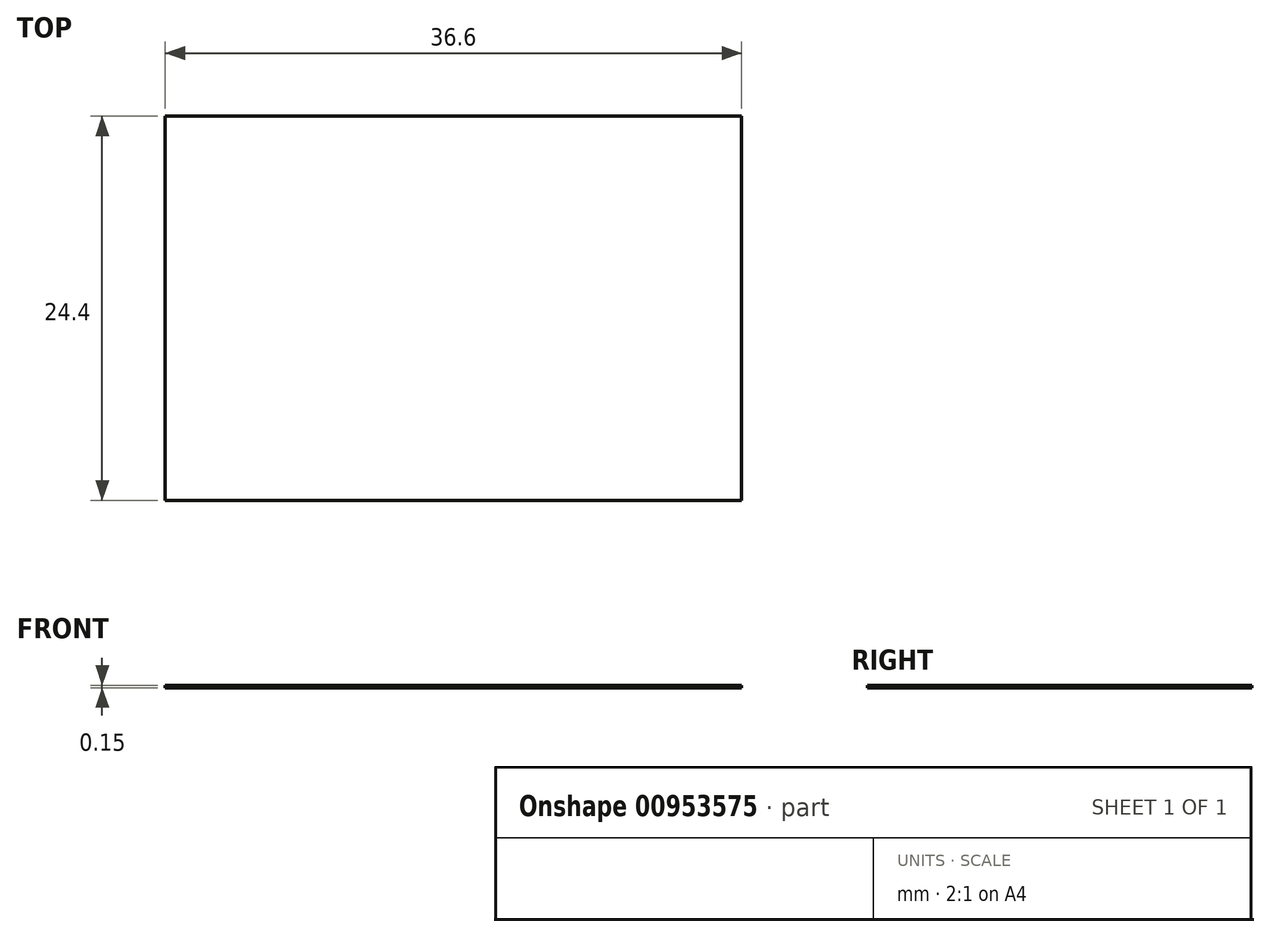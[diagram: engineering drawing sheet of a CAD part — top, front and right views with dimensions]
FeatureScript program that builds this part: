
annotation { "Feature Type Name" : "Feature", "Feature Type Description" : "" }
export const myFeature = defineFeature(function(context is Context, id is Id, definition is map)
    precondition{}
    {
        {
            var Q0;
            Q0=qCreatedBy(makeId("Top.planeOp"),FACE);
            var sketch = newSketch(context, id + "F0", { "sketchPlane" : qUnion([Q0])});
            skLineSegment(sketch, "E0.bottom", {"start": v(1.19, 0.06) * mm, "end": v(37.79, 0.06) * mm});
            skLineSegment(sketch, "E0.top", {"start": v(1.19, -24.34) * mm, "end": v(37.79, -24.34) * mm});
            skLineSegment(sketch, "E0.left", {"start": v(1.19, 0.06) * mm, "end": v(1.19, -24.34) * mm});
            skLineSegment(sketch, "E0.right", {"start": v(37.79, 0.06) * mm, "end": v(37.79, -24.34) * mm});
            skPoint(sketch, "E1", {"position": v(1.95, 0.06) * mm});
            skPoint(sketch, "E2", {"position": v(37.03, 0.06) * mm});
            skPoint(sketch, "E3", {"position": v(1.19, -23.58) * mm});
            skPoint(sketch, "E4", {"position": v(1.19, -0.7) * mm});
            skPoint(sketch, "E5", {"position": v(13.39, 0.06) * mm});
            skPoint(sketch, "E6", {"position": v(25.59, -24.34) * mm});
            skPoint(sketch, "E7", {"position": v(25.59, 0.06) * mm});
            skPoint(sketch, "E8", {"position": v(37.79, -24.34) * mm});
            skLineSegment(sketch, "E9", {"start": v(1.19, -0.7) * mm, "end": v(37.79, -0.7) * mm});
            skLineSegment(sketch, "E10", {"start": v(1.19, -23.58) * mm, "end": v(37.79, -23.58) * mm});
            skLineSegment(sketch, "E11", {"start": v(1.95, 0.06) * mm, "end": v(1.95, -24.34) * mm});
            skLineSegment(sketch, "E12", {"start": v(37.03, 0.06) * mm, "end": v(37.03, -24.34) * mm});
            skPoint(sketch, "E13", {"position": v(1.19, -12.14) * mm});
            skPoint(sketch, "E14", {"position": v(37.79, -12.14) * mm});
            skLineSegment(sketch, "E15", {"start": v(1.95, -12.14) * mm, "end": v(25.59, -12.14) * mm});
            skLineSegment(sketch, "E16", {"start": v(25.59, -24.34) * mm, "end": v(25.59, -0.7) * mm});
            skLineSegment(sketch, "E17", {"start": v(25.59, -0.7) * mm, "end": v(25.59, 0.06) * mm});
            skLineSegment(sketch, "E18", {"start": v(1.19, -12.14) * mm, "end": v(1.95, -12.14) * mm});
            skLineSegment(sketch, "E19.trimOffspring", {"start": v(37.03, -12.14) * mm, "end": v(37.79, -12.14) * mm});
            skPoint(sketch, "E20", {"position": v(37.79, -11.64) * mm});
            skPoint(sketch, "E21", {"position": v(37.79, -12.64) * mm});
            skLineSegment(sketch, "E22", {"start": v(13.39, 0.06) * mm, "end": v(12.81, -24.34) * mm});
            skPoint(sketch, "E23", {"position": v(1.69, 0.06) * mm});
            skPoint(sketch, "E24", {"position": v(12.89, 0.06) * mm});
            skPoint(sketch, "E25", {"position": v(13.89, 0.06) * mm});
            skPoint(sketch, "E26", {"position": v(25.09, 0.06) * mm});
            skPoint(sketch, "E27", {"position": v(26.09, 0.06) * mm});
            skPoint(sketch, "E28", {"position": v(37.29, 0.06) * mm});
            skPoint(sketch, "E29", {"position": v(37.79, -1.2) * mm});
            skPoint(sketch, "E30", {"position": v(37.79, -23.08) * mm});
            skLineSegment(sketch, "E31", {"start": v(1.69, 0.06) * mm, "end": v(1.69, -24.34) * mm});
            skLineSegment(sketch, "E32", {"start": v(12.89, 0.06) * mm, "end": v(12.31, -24.34) * mm});
            skLineSegment(sketch, "E33", {"start": v(13.89, 0.06) * mm, "end": v(13.31, -24.34) * mm});
            skLineSegment(sketch, "E34", {"start": v(25.09, 0.06) * mm, "end": v(25.09, -24.34) * mm});
            skLineSegment(sketch, "E35", {"start": v(26.09, 0.06) * mm, "end": v(26.09, -24.34) * mm});
            skLineSegment(sketch, "E36", {"start": v(37.29, 0.06) * mm, "end": v(37.29, -24.34) * mm});
            skLineSegment(sketch, "E37", {"start": v(37.79, -1.2) * mm, "end": v(1.19, -1.2) * mm});
            skLineSegment(sketch, "E38", {"start": v(37.79, -23.08) * mm, "end": v(1.19, -23.08) * mm});
            skSolve(sketch);
        }
        {
            var Q0;
            {var subQ0=sQuery(id+"F0.wireOp",EDGE,"E18");var subQ1=sQuery(id+"F0.wireOp",EDGE,"E0.left");var subQ2=makeQuery(id+"F0.imprint","INTERSECT",VERTEX,{"derivedFrom":[subQ1,subQ0]});Q0=makeQuery(id+"F0.imprint","IMPRINT",FACE,{"disambiguationData":[TD([[makeQuery(id+"F0.imprint","IMPRINT",EDGE,{"disambiguationData":[TD([[subQ2,-1.0]])],"derivedFrom":subQ1}),1.0]])]});}
            var Q1;
            {var subQ0=sQuery(id+"F0.wireOp",EDGE,"E32");var subQ1=sQuery(id+"F0.wireOp",EDGE,"E9");var subQ2=makeQuery(id+"F0.imprint","INTERSECT",VERTEX,{"derivedFrom":[subQ1,subQ0]});Q1=makeQuery(id+"F0.imprint","IMPRINT",FACE,{"disambiguationData":[TD([[makeQuery(id+"F0.imprint","IMPRINT",EDGE,{"disambiguationData":[TD([[subQ2,-1.0]])],"derivedFrom":subQ1}),-1.0]])]});}
            var Q2;
            {var subQ0=sQuery(id+"F0.wireOp",EDGE,"E12");var subQ1=sQuery(id+"F0.wireOp",EDGE,"E0.bottom");var subQ2=makeQuery(id+"F0.imprint","INTERSECT",VERTEX,{"derivedFrom":[subQ1,subQ0]});Q2=makeQuery(id+"F0.imprint","IMPRINT",FACE,{"disambiguationData":[TD([[makeQuery(id+"F0.imprint","IMPRINT",EDGE,{"disambiguationData":[TD([[subQ2,1.0]])],"derivedFrom":subQ1}),-1.0]])]});}
            var Q3;
            {var subQ0=sQuery(id+"F0.wireOp",EDGE,"E12");var subQ1=sQuery(id+"F0.wireOp",EDGE,"E0.top");var subQ2=makeQuery(id+"F0.imprint","INTERSECT",VERTEX,{"derivedFrom":[subQ1,subQ0]});Q3=makeQuery(id+"F0.imprint","IMPRINT",FACE,{"disambiguationData":[TD([[makeQuery(id+"F0.imprint","IMPRINT",EDGE,{"disambiguationData":[TD([[subQ2,1.0]])],"derivedFrom":subQ1}),1.0]])]});}
            var Q4;
            {var subQ0=sQuery(id+"F0.wireOp",EDGE,"E15");var subQ5=sQuery(id+"F0.wireOp",EDGE,"E32");var subQ6=makeQuery(id+"F0.imprint","INTERSECT",VERTEX,{"derivedFrom":[subQ0,subQ5]});Q4=makeQuery(id+"F0.imprint","IMPRINT",FACE,{"disambiguationData":[TD([[makeQuery(id+"F0.imprint","IMPRINT",EDGE,{"disambiguationData":[TD([[subQ6,-1.0]])],"derivedFrom":subQ5}),-1.0]])]});}
            var Q5;
            {var subQ0=sQuery(id+"F0.wireOp",EDGE,"E16");var subQ1=sQuery(id+"F0.wireOp",EDGE,"E15");var subQ2=makeQuery(id+"F0.imprint","INTERSECT",VERTEX,{"derivedFrom":[subQ1,subQ0]});Q5=makeQuery(id+"F0.imprint","IMPRINT",FACE,{"disambiguationData":[TD([[makeQuery(id+"F0.imprint","IMPRINT",EDGE,{"disambiguationData":[TD([[subQ2,1.0]])],"derivedFrom":subQ1}),-1.0]])]});}
            var Q6;
            {var subQ0=sQuery(id+"F0.wireOp",EDGE,"E22");var subQ1=sQuery(id+"F0.wireOp",EDGE,"E15");var subQ2=makeQuery(id+"F0.imprint","INTERSECT",VERTEX,{"derivedFrom":[subQ1,subQ0]});Q6=makeQuery(id+"F0.imprint","IMPRINT",FACE,{"disambiguationData":[TD([[makeQuery(id+"F0.imprint","IMPRINT",EDGE,{"disambiguationData":[TD([[subQ2,-1.0]])],"derivedFrom":subQ1}),1.0]])]});}
            var Q7;
            {var subQ0=sQuery(id+"F0.wireOp",EDGE,"E18");var subQ1=sQuery(id+"F0.wireOp",EDGE,"E0.left");var subQ2=makeQuery(id+"F0.imprint","INTERSECT",VERTEX,{"derivedFrom":[subQ1,subQ0]});Q7=makeQuery(id+"F0.imprint","IMPRINT",FACE,{"disambiguationData":[TD([[makeQuery(id+"F0.imprint","IMPRINT",EDGE,{"disambiguationData":[TD([[subQ2,1.0]])],"derivedFrom":subQ1}),1.0]])]});}
            var Q8;
            {var subQ0=sQuery(id+"F0.wireOp",EDGE,"E22");var subQ1=sQuery(id+"F0.wireOp",EDGE,"E15");var subQ2=makeQuery(id+"F0.imprint","INTERSECT",VERTEX,{"derivedFrom":[subQ1,subQ0]});Q8=makeQuery(id+"F0.imprint","IMPRINT",FACE,{"disambiguationData":[TD([[makeQuery(id+"F0.imprint","IMPRINT",EDGE,{"disambiguationData":[TD([[subQ2,-1.0]])],"derivedFrom":subQ1}),-1.0]])]});}
            var Q9;
            {var subQ0=sQuery(id+"F0.wireOp",EDGE,"E11");var subQ1=sQuery(id+"F0.wireOp",EDGE,"E9");var subQ2=makeQuery(id+"F0.imprint","INTERSECT",VERTEX,{"derivedFrom":[subQ1,subQ0]});Q9=makeQuery(id+"F0.imprint","IMPRINT",FACE,{"disambiguationData":[TD([[makeQuery(id+"F0.imprint","IMPRINT",EDGE,{"disambiguationData":[TD([[subQ2,-1.0]])],"derivedFrom":subQ1}),-1.0]])]});}
            var Q10;
            {var subQ0=sQuery(id+"F0.wireOp",EDGE,"E11");var subQ1=sQuery(id+"F0.wireOp",EDGE,"E0.bottom");var subQ2=makeQuery(id+"F0.imprint","INTERSECT",VERTEX,{"derivedFrom":[subQ1,subQ0]});Q10=makeQuery(id+"F0.imprint","IMPRINT",FACE,{"disambiguationData":[TD([[makeQuery(id+"F0.imprint","IMPRINT",EDGE,{"disambiguationData":[TD([[subQ2,-1.0]])],"derivedFrom":subQ1}),-1.0]])]});}
            var Q11;
            {var subQ0=sQuery(id+"F0.wireOp",EDGE,"E32");var subQ1=sQuery(id+"F0.wireOp",EDGE,"E10");var subQ2=makeQuery(id+"F0.imprint","INTERSECT",VERTEX,{"derivedFrom":[subQ1,subQ0]});Q11=makeQuery(id+"F0.imprint","IMPRINT",FACE,{"disambiguationData":[TD([[makeQuery(id+"F0.imprint","IMPRINT",EDGE,{"disambiguationData":[TD([[subQ2,-1.0]])],"derivedFrom":subQ1}),1.0]])]});}
            var Q12;
            {var subQ0=sQuery(id+"F0.wireOp",EDGE,"E33");var subQ1=sQuery(id+"F0.wireOp",EDGE,"E0.top");var subQ2=makeQuery(id+"F0.imprint","INTERSECT",VERTEX,{"derivedFrom":[subQ1,subQ0]});Q12=makeQuery(id+"F0.imprint","IMPRINT",FACE,{"disambiguationData":[TD([[makeQuery(id+"F0.imprint","IMPRINT",EDGE,{"disambiguationData":[TD([[subQ2,-1.0]])],"derivedFrom":subQ1}),1.0]])]});}
            var Q13;
            {var subQ0=sQuery(id+"F0.wireOp",EDGE,"E19.trimOffspring");var subQ1=sQuery(id+"F0.wireOp",EDGE,"E0.right");var subQ2=makeQuery(id+"F0.imprint","INTERSECT",VERTEX,{"derivedFrom":[subQ1,subQ0]});Q13=makeQuery(id+"F0.imprint","IMPRINT",FACE,{"disambiguationData":[TD([[makeQuery(id+"F0.imprint","IMPRINT",EDGE,{"disambiguationData":[TD([[subQ2,-1.0]])],"derivedFrom":subQ1}),-1.0]])]});}
            var Q14;
            {var subQ0=sQuery(id+"F0.wireOp",EDGE,"E22");var subQ1=sQuery(id+"F0.wireOp",EDGE,"E0.top");var subQ2=makeQuery(id+"F0.imprint","INTERSECT",VERTEX,{"derivedFrom":[subQ1,subQ0]});Q14=makeQuery(id+"F0.imprint","IMPRINT",FACE,{"disambiguationData":[TD([[makeQuery(id+"F0.imprint","IMPRINT",EDGE,{"disambiguationData":[TD([[subQ2,1.0]])],"derivedFrom":subQ1}),1.0]])]});}
            var Q15;
            {var subQ0=sQuery(id+"F0.wireOp",EDGE,"E11");var subQ1=sQuery(id+"F0.wireOp",EDGE,"E0.top");var subQ2=makeQuery(id+"F0.imprint","INTERSECT",VERTEX,{"derivedFrom":[subQ1,subQ0]});Q15=makeQuery(id+"F0.imprint","IMPRINT",FACE,{"disambiguationData":[TD([[makeQuery(id+"F0.imprint","IMPRINT",EDGE,{"disambiguationData":[TD([[subQ2,-1.0]])],"derivedFrom":subQ1}),1.0]])]});}
            var Q16;
            {var subQ0=sQuery(id+"F0.wireOp",EDGE,"E33");var subQ1=sQuery(id+"F0.wireOp",EDGE,"E0.bottom");var subQ2=makeQuery(id+"F0.imprint","INTERSECT",VERTEX,{"derivedFrom":[subQ1,subQ0]});Q16=makeQuery(id+"F0.imprint","IMPRINT",FACE,{"disambiguationData":[TD([[makeQuery(id+"F0.imprint","IMPRINT",EDGE,{"disambiguationData":[TD([[subQ2,-1.0]])],"derivedFrom":subQ1}),-1.0]])]});}
            var Q17;
            {var subQ1=sQuery(id+"F0.wireOp",EDGE,"E12");var subQ8=makeQuery(id+"F0.imprint","INTERSECT",VERTEX,{"derivedFrom":[subQ1,sQuery(id+"F0.wireOp",EDGE,"E19.trimOffspring")]});Q17=makeQuery(id+"F0.imprint","IMPRINT",FACE,{"disambiguationData":[TD([[makeQuery(id+"F0.imprint","IMPRINT",EDGE,{"disambiguationData":[TD([[subQ8,1.0]])],"derivedFrom":subQ1}),-1.0]])]});}
            var Q18;
            {var subQ1=sQuery(id+"F0.wireOp",EDGE,"E16");var subQ8=makeQuery(id+"F0.imprint","INTERSECT",VERTEX,{"derivedFrom":[sQuery(id+"F0.wireOp",EDGE,"E15"),subQ1]});Q18=makeQuery(id+"F0.imprint","IMPRINT",FACE,{"disambiguationData":[TD([[makeQuery(id+"F0.imprint","IMPRINT",EDGE,{"disambiguationData":[TD([[subQ8,1.0]])],"derivedFrom":subQ1}),-1.0]])]});}
            var Q19;
            {var subQ0=sQuery(id+"F0.wireOp",EDGE,"E15");var subQ5=sQuery(id+"F0.wireOp",EDGE,"E32");var subQ6=makeQuery(id+"F0.imprint","INTERSECT",VERTEX,{"derivedFrom":[subQ0,subQ5]});Q19=makeQuery(id+"F0.imprint","IMPRINT",FACE,{"disambiguationData":[TD([[makeQuery(id+"F0.imprint","IMPRINT",EDGE,{"disambiguationData":[TD([[subQ6,1.0]])],"derivedFrom":subQ5}),-1.0]])]});}
            var Q20;
            {var subQ0=sQuery(id+"F0.wireOp",EDGE,"E16");var subQ1=sQuery(id+"F0.wireOp",EDGE,"E15");var subQ2=makeQuery(id+"F0.imprint","INTERSECT",VERTEX,{"derivedFrom":[subQ1,subQ0]});Q20=makeQuery(id+"F0.imprint","IMPRINT",FACE,{"disambiguationData":[TD([[makeQuery(id+"F0.imprint","IMPRINT",EDGE,{"disambiguationData":[TD([[subQ2,1.0]])],"derivedFrom":subQ1}),1.0]])]});}
            var Q21;
            {var subQ0=sQuery(id+"F0.wireOp",EDGE,"E16");var subQ1=sQuery(id+"F0.wireOp",EDGE,"E10");var subQ2=makeQuery(id+"F0.imprint","INTERSECT",VERTEX,{"derivedFrom":[subQ1,subQ0]});Q21=makeQuery(id+"F0.imprint","IMPRINT",FACE,{"disambiguationData":[TD([[makeQuery(id+"F0.imprint","IMPRINT",EDGE,{"disambiguationData":[TD([[subQ2,-1.0]])],"derivedFrom":subQ1}),1.0]])]});}
            var Q22;
            {var subQ0=sQuery(id+"F0.wireOp",EDGE,"E35");var subQ1=sQuery(id+"F0.wireOp",EDGE,"E9");var subQ2=makeQuery(id+"F0.imprint","INTERSECT",VERTEX,{"derivedFrom":[subQ1,subQ0]});Q22=makeQuery(id+"F0.imprint","IMPRINT",FACE,{"disambiguationData":[TD([[makeQuery(id+"F0.imprint","IMPRINT",EDGE,{"disambiguationData":[TD([[subQ2,-1.0]])],"derivedFrom":subQ1}),-1.0]])]});}
            var Q23;
            {var subQ0=sQuery(id+"F0.wireOp",EDGE,"E32");var subQ1=sQuery(id+"F0.wireOp",EDGE,"E15");var subQ2=makeQuery(id+"F0.imprint","INTERSECT",VERTEX,{"derivedFrom":[subQ1,subQ0]});Q23=makeQuery(id+"F0.imprint","IMPRINT",FACE,{"disambiguationData":[TD([[makeQuery(id+"F0.imprint","IMPRINT",EDGE,{"disambiguationData":[TD([[subQ2,-1.0]])],"derivedFrom":subQ1}),-1.0]])]});}
            var Q24;
            {var subQ0=sQuery(id+"F0.wireOp",EDGE,"E19.trimOffspring");var subQ1=sQuery(id+"F0.wireOp",EDGE,"E0.right");var subQ2=makeQuery(id+"F0.imprint","INTERSECT",VERTEX,{"derivedFrom":[subQ1,subQ0]});Q24=makeQuery(id+"F0.imprint","IMPRINT",FACE,{"disambiguationData":[TD([[makeQuery(id+"F0.imprint","IMPRINT",EDGE,{"disambiguationData":[TD([[subQ2,1.0]])],"derivedFrom":subQ1}),-1.0]])]});}
            var Q25;
            {var subQ0=sQuery(id+"F0.wireOp",EDGE,"E22");var subQ1=sQuery(id+"F0.wireOp",EDGE,"E9");var subQ2=makeQuery(id+"F0.imprint","INTERSECT",VERTEX,{"derivedFrom":[subQ1,subQ0]});Q25=makeQuery(id+"F0.imprint","IMPRINT",FACE,{"disambiguationData":[TD([[makeQuery(id+"F0.imprint","IMPRINT",EDGE,{"disambiguationData":[TD([[subQ2,-1.0]])],"derivedFrom":subQ1}),-1.0]])]});}
            var Q26;
            {var subQ0=sQuery(id+"F0.wireOp",EDGE,"E11");var subQ1=sQuery(id+"F0.wireOp",EDGE,"E10");var subQ2=makeQuery(id+"F0.imprint","INTERSECT",VERTEX,{"derivedFrom":[subQ1,subQ0]});Q26=makeQuery(id+"F0.imprint","IMPRINT",FACE,{"disambiguationData":[TD([[makeQuery(id+"F0.imprint","IMPRINT",EDGE,{"disambiguationData":[TD([[subQ2,-1.0]])],"derivedFrom":subQ1}),1.0]])]});}
            var Q27;
            {var subQ0=sQuery(id+"F0.wireOp",EDGE,"E22");var subQ1=sQuery(id+"F0.wireOp",EDGE,"E10");var subQ2=makeQuery(id+"F0.imprint","INTERSECT",VERTEX,{"derivedFrom":[subQ1,subQ0]});Q27=makeQuery(id+"F0.imprint","IMPRINT",FACE,{"disambiguationData":[TD([[makeQuery(id+"F0.imprint","IMPRINT",EDGE,{"disambiguationData":[TD([[subQ2,-1.0]])],"derivedFrom":subQ1}),1.0]])]});}
            var Q28;
            {var subQ0=sQuery(id+"F0.wireOp",EDGE,"E33");var subQ1=sQuery(id+"F0.wireOp",EDGE,"E10");var subQ2=makeQuery(id+"F0.imprint","INTERSECT",VERTEX,{"derivedFrom":[subQ1,subQ0]});Q28=makeQuery(id+"F0.imprint","IMPRINT",FACE,{"disambiguationData":[TD([[makeQuery(id+"F0.imprint","IMPRINT",EDGE,{"disambiguationData":[TD([[subQ2,-1.0]])],"derivedFrom":subQ1}),1.0]])]});}
            var Q29;
            {var subQ0=sQuery(id+"F0.wireOp",EDGE,"E32");var subQ1=sQuery(id+"F0.wireOp",EDGE,"E15");var subQ2=makeQuery(id+"F0.imprint","INTERSECT",VERTEX,{"derivedFrom":[subQ1,subQ0]});Q29=makeQuery(id+"F0.imprint","IMPRINT",FACE,{"disambiguationData":[TD([[makeQuery(id+"F0.imprint","IMPRINT",EDGE,{"disambiguationData":[TD([[subQ2,-1.0]])],"derivedFrom":subQ1}),1.0]])]});}
            var Q30;
            {var subQ0=sQuery(id+"F0.wireOp",EDGE,"E34");var subQ1=sQuery(id+"F0.wireOp",EDGE,"E10");var subQ2=makeQuery(id+"F0.imprint","INTERSECT",VERTEX,{"derivedFrom":[subQ1,subQ0]});Q30=makeQuery(id+"F0.imprint","IMPRINT",FACE,{"disambiguationData":[TD([[makeQuery(id+"F0.imprint","IMPRINT",EDGE,{"disambiguationData":[TD([[subQ2,-1.0]])],"derivedFrom":subQ1}),1.0]])]});}
            var Q31;
            {var subQ0=sQuery(id+"F0.wireOp",EDGE,"E35");var subQ1=sQuery(id+"F0.wireOp",EDGE,"E10");var subQ2=makeQuery(id+"F0.imprint","INTERSECT",VERTEX,{"derivedFrom":[subQ1,subQ0]});Q31=makeQuery(id+"F0.imprint","IMPRINT",FACE,{"disambiguationData":[TD([[makeQuery(id+"F0.imprint","IMPRINT",EDGE,{"disambiguationData":[TD([[subQ2,-1.0]])],"derivedFrom":subQ1}),1.0]])]});}
            var Q32;
            {var subQ0=sQuery(id+"F0.wireOp",EDGE,"E33");var subQ1=sQuery(id+"F0.wireOp",EDGE,"E9");var subQ2=makeQuery(id+"F0.imprint","INTERSECT",VERTEX,{"derivedFrom":[subQ1,subQ0]});Q32=makeQuery(id+"F0.imprint","IMPRINT",FACE,{"disambiguationData":[TD([[makeQuery(id+"F0.imprint","IMPRINT",EDGE,{"disambiguationData":[TD([[subQ2,-1.0]])],"derivedFrom":subQ1}),-1.0]])]});}
            var Q33;
            {var subQ0=sQuery(id+"F0.wireOp",EDGE,"E22");var subQ1=sQuery(id+"F0.wireOp",EDGE,"E0.top");var subQ2=makeQuery(id+"F0.imprint","INTERSECT",VERTEX,{"derivedFrom":[subQ1,subQ0]});Q33=makeQuery(id+"F0.imprint","IMPRINT",FACE,{"disambiguationData":[TD([[makeQuery(id+"F0.imprint","IMPRINT",EDGE,{"disambiguationData":[TD([[subQ2,-1.0]])],"derivedFrom":subQ1}),1.0]])]});}
            var Q34;
            {var subQ0=sQuery(id+"F0.wireOp",EDGE,"E33");var subQ1=sQuery(id+"F0.wireOp",EDGE,"E15");var subQ2=makeQuery(id+"F0.imprint","INTERSECT",VERTEX,{"derivedFrom":[subQ1,subQ0]});Q34=makeQuery(id+"F0.imprint","IMPRINT",FACE,{"disambiguationData":[TD([[makeQuery(id+"F0.imprint","IMPRINT",EDGE,{"disambiguationData":[TD([[subQ2,-1.0]])],"derivedFrom":subQ1}),-1.0]])]});}
            var Q35;
            {var subQ0=sQuery(id+"F0.wireOp",EDGE,"E33");var subQ1=sQuery(id+"F0.wireOp",EDGE,"E15");var subQ2=makeQuery(id+"F0.imprint","INTERSECT",VERTEX,{"derivedFrom":[subQ1,subQ0]});Q35=makeQuery(id+"F0.imprint","IMPRINT",FACE,{"disambiguationData":[TD([[makeQuery(id+"F0.imprint","IMPRINT",EDGE,{"disambiguationData":[TD([[subQ2,-1.0]])],"derivedFrom":subQ1}),1.0]])]});}
            var Q36;
            {var subQ0=sQuery(id+"F0.wireOp",EDGE,"E11");var subQ1=sQuery(id+"F0.wireOp",EDGE,"E0.top");var subQ2=makeQuery(id+"F0.imprint","INTERSECT",VERTEX,{"derivedFrom":[subQ1,subQ0]});Q36=makeQuery(id+"F0.imprint","IMPRINT",FACE,{"disambiguationData":[TD([[makeQuery(id+"F0.imprint","IMPRINT",EDGE,{"disambiguationData":[TD([[subQ2,1.0]])],"derivedFrom":subQ1}),1.0]])]});}
            var Q37;
            {var subQ0=sQuery(id+"F0.wireOp",EDGE,"E9");var subQ1=sQuery(id+"F0.wireOp",EDGE,"E0.right");var subQ2=makeQuery(id+"F0.imprint","INTERSECT",VERTEX,{"derivedFrom":[subQ1,subQ0]});Q37=makeQuery(id+"F0.imprint","IMPRINT",FACE,{"disambiguationData":[TD([[makeQuery(id+"F0.imprint","IMPRINT",EDGE,{"disambiguationData":[TD([[subQ2,-1.0]])],"derivedFrom":subQ1}),-1.0]])]});}
            var Q38;
            {var subQ0=sQuery(id+"F0.wireOp",EDGE,"E22");var subQ1=sQuery(id+"F0.wireOp",EDGE,"E0.bottom");var subQ2=makeQuery(id+"F0.imprint","INTERSECT",VERTEX,{"derivedFrom":[subQ1,subQ0]});Q38=makeQuery(id+"F0.imprint","IMPRINT",FACE,{"disambiguationData":[TD([[makeQuery(id+"F0.imprint","IMPRINT",EDGE,{"disambiguationData":[TD([[subQ2,1.0]])],"derivedFrom":subQ1}),-1.0]])]});}
            var Q39;
            {var subQ0=sQuery(id+"F0.wireOp",EDGE,"E0.right");var subQ1=sQuery(id+"F0.wireOp",EDGE,"E0.top");var subQ2=makeQuery(id+"F0.imprint","INTERSECT",VERTEX,{"derivedFrom":[subQ1,subQ0]});Q39=makeQuery(id+"F0.imprint","IMPRINT",FACE,{"disambiguationData":[TD([[makeQuery(id+"F0.imprint","IMPRINT",EDGE,{"disambiguationData":[TD([[subQ2,1.0]])],"derivedFrom":subQ1}),1.0]])]});}
            var Q40;
            {var subQ0=sQuery(id+"F0.wireOp",EDGE,"E10");var subQ1=sQuery(id+"F0.wireOp",EDGE,"E0.left");var subQ2=makeQuery(id+"F0.imprint","INTERSECT",VERTEX,{"derivedFrom":[subQ1,subQ0]});Q40=makeQuery(id+"F0.imprint","IMPRINT",FACE,{"disambiguationData":[TD([[makeQuery(id+"F0.imprint","IMPRINT",EDGE,{"disambiguationData":[TD([[subQ2,1.0]])],"derivedFrom":subQ1}),1.0]])]});}
            var Q41;
            {var subQ0=sQuery(id+"F0.wireOp",EDGE,"E19.trimOffspring");var subQ1=sQuery(id+"F0.wireOp",EDGE,"E12");var subQ2=makeQuery(id+"F0.imprint","INTERSECT",VERTEX,{"derivedFrom":[subQ1,subQ0]});Q41=makeQuery(id+"F0.imprint","IMPRINT",FACE,{"disambiguationData":[TD([[makeQuery(id+"F0.imprint","IMPRINT",EDGE,{"disambiguationData":[TD([[subQ2,-1.0]])],"derivedFrom":subQ1}),1.0]])]});}
            var Q42;
            {var subQ0=sQuery(id+"F0.wireOp",EDGE,"E0.left");var subQ1=sQuery(id+"F0.wireOp",EDGE,"E0.top");var subQ2=makeQuery(id+"F0.imprint","INTERSECT",VERTEX,{"derivedFrom":[subQ1,subQ0]});Q42=makeQuery(id+"F0.imprint","IMPRINT",FACE,{"disambiguationData":[TD([[makeQuery(id+"F0.imprint","IMPRINT",EDGE,{"disambiguationData":[TD([[subQ2,-1.0]])],"derivedFrom":subQ1}),1.0]])]});}
            var Q43;
            {var subQ0=sQuery(id+"F0.wireOp",EDGE,"E18");var subQ5=sQuery(id+"F0.wireOp",EDGE,"E31");var subQ7=makeQuery(id+"F0.imprint","INTERSECT",VERTEX,{"derivedFrom":[subQ0,subQ5]});Q43=makeQuery(id+"F0.imprint","IMPRINT",FACE,{"disambiguationData":[TD([[makeQuery(id+"F0.imprint","IMPRINT",EDGE,{"disambiguationData":[TD([[subQ7,-1.0]])],"derivedFrom":subQ5}),1.0]])]});}
            var Q44;
            {var subQ0=sQuery(id+"F0.wireOp",EDGE,"E0.right");var subQ1=sQuery(id+"F0.wireOp",EDGE,"E0.bottom");var subQ2=makeQuery(id+"F0.imprint","INTERSECT",VERTEX,{"derivedFrom":[subQ1,subQ0]});Q44=makeQuery(id+"F0.imprint","IMPRINT",FACE,{"disambiguationData":[TD([[makeQuery(id+"F0.imprint","IMPRINT",EDGE,{"disambiguationData":[TD([[subQ2,1.0]])],"derivedFrom":subQ1}),-1.0]])]});}
            var Q45;
            {var subQ0=sQuery(id+"F0.wireOp",EDGE,"E12");var subQ1=sQuery(id+"F0.wireOp",EDGE,"E10");var subQ2=makeQuery(id+"F0.imprint","INTERSECT",VERTEX,{"derivedFrom":[subQ1,subQ0]});Q45=makeQuery(id+"F0.imprint","IMPRINT",FACE,{"disambiguationData":[TD([[makeQuery(id+"F0.imprint","IMPRINT",EDGE,{"disambiguationData":[TD([[subQ2,-1.0]])],"derivedFrom":subQ1}),1.0]])]});}
            var Q46;
            {var subQ1=sQuery(id+"F0.wireOp",EDGE,"E9");var subQ3=sQuery(id+"F0.wireOp",EDGE,"E34");var subQ4=makeQuery(id+"F0.imprint","INTERSECT",VERTEX,{"derivedFrom":[subQ1,subQ3]});Q46=makeQuery(id+"F0.imprint","IMPRINT",FACE,{"disambiguationData":[TD([[makeQuery(id+"F0.imprint","IMPRINT",EDGE,{"disambiguationData":[TD([[subQ4,-1.0]])],"derivedFrom":subQ3}),1.0]])]});}
            var Q47;
            {var subQ0=sQuery(id+"F0.wireOp",EDGE,"E10");var subQ1=sQuery(id+"F0.wireOp",EDGE,"E0.right");var subQ2=makeQuery(id+"F0.imprint","INTERSECT",VERTEX,{"derivedFrom":[subQ1,subQ0]});Q47=makeQuery(id+"F0.imprint","IMPRINT",FACE,{"disambiguationData":[TD([[makeQuery(id+"F0.imprint","IMPRINT",EDGE,{"disambiguationData":[TD([[subQ2,1.0]])],"derivedFrom":subQ1}),-1.0]])]});}
            var Q48;
            {var subQ0=sQuery(id+"F0.wireOp",EDGE,"E12");var subQ1=sQuery(id+"F0.wireOp",EDGE,"E9");var subQ2=makeQuery(id+"F0.imprint","INTERSECT",VERTEX,{"derivedFrom":[subQ1,subQ0]});Q48=makeQuery(id+"F0.imprint","IMPRINT",FACE,{"disambiguationData":[TD([[makeQuery(id+"F0.imprint","IMPRINT",EDGE,{"disambiguationData":[TD([[subQ2,-1.0]])],"derivedFrom":subQ1}),-1.0]])]});}
            var Q49;
            {var subQ0=sQuery(id+"F0.wireOp",EDGE,"E17");Q49=makeQuery(id+"F0.imprint","IMPRINT",FACE,{"disambiguationData":[TD([[makeQuery(id+"F0.imprint","IMPRINT",EDGE,{"derivedFrom":subQ0}),1.0]])]});}
            var Q50;
            {var subQ0=sQuery(id+"F0.wireOp",EDGE,"E18");var subQ5=sQuery(id+"F0.wireOp",EDGE,"E31");var subQ7=makeQuery(id+"F0.imprint","INTERSECT",VERTEX,{"derivedFrom":[subQ0,subQ5]});Q50=makeQuery(id+"F0.imprint","IMPRINT",FACE,{"disambiguationData":[TD([[makeQuery(id+"F0.imprint","IMPRINT",EDGE,{"disambiguationData":[TD([[subQ7,1.0]])],"derivedFrom":subQ5}),1.0]])]});}
            var Q51;
            {var subQ0=sQuery(id+"F0.wireOp",EDGE,"E22");var subQ1=sQuery(id+"F0.wireOp",EDGE,"E0.bottom");var subQ2=makeQuery(id+"F0.imprint","INTERSECT",VERTEX,{"derivedFrom":[subQ1,subQ0]});Q51=makeQuery(id+"F0.imprint","IMPRINT",FACE,{"disambiguationData":[TD([[makeQuery(id+"F0.imprint","IMPRINT",EDGE,{"disambiguationData":[TD([[subQ2,-1.0]])],"derivedFrom":subQ1}),-1.0]])]});}
            var Q52;
            {var subQ0=sQuery(id+"F0.wireOp",EDGE,"E31");var subQ1=sQuery(id+"F0.wireOp",EDGE,"E10");var subQ2=makeQuery(id+"F0.imprint","INTERSECT",VERTEX,{"derivedFrom":[subQ1,subQ0]});Q52=makeQuery(id+"F0.imprint","IMPRINT",FACE,{"disambiguationData":[TD([[makeQuery(id+"F0.imprint","IMPRINT",EDGE,{"disambiguationData":[TD([[subQ2,-1.0]])],"derivedFrom":subQ1}),1.0]])]});}
            var Q53;
            {var subQ0=sQuery(id+"F0.wireOp",EDGE,"E0.left");var subQ1=sQuery(id+"F0.wireOp",EDGE,"E0.bottom");var subQ2=makeQuery(id+"F0.imprint","INTERSECT",VERTEX,{"derivedFrom":[subQ1,subQ0]});Q53=makeQuery(id+"F0.imprint","IMPRINT",FACE,{"disambiguationData":[TD([[makeQuery(id+"F0.imprint","IMPRINT",EDGE,{"disambiguationData":[TD([[subQ2,-1.0]])],"derivedFrom":subQ1}),-1.0]])]});}
            var Q54;
            {var subQ0=sQuery(id+"F0.wireOp",EDGE,"E12");var subQ1=sQuery(id+"F0.wireOp",EDGE,"E0.top");var subQ2=makeQuery(id+"F0.imprint","INTERSECT",VERTEX,{"derivedFrom":[subQ1,subQ0]});Q54=makeQuery(id+"F0.imprint","IMPRINT",FACE,{"disambiguationData":[TD([[makeQuery(id+"F0.imprint","IMPRINT",EDGE,{"disambiguationData":[TD([[subQ2,-1.0]])],"derivedFrom":subQ1}),1.0]])]});}
            var Q55;
            {var subQ0=sQuery(id+"F0.wireOp",EDGE,"E9");var subQ1=sQuery(id+"F0.wireOp",EDGE,"E0.left");var subQ2=makeQuery(id+"F0.imprint","INTERSECT",VERTEX,{"derivedFrom":[subQ1,subQ0]});Q55=makeQuery(id+"F0.imprint","IMPRINT",FACE,{"disambiguationData":[TD([[makeQuery(id+"F0.imprint","IMPRINT",EDGE,{"disambiguationData":[TD([[subQ2,-1.0]])],"derivedFrom":subQ1}),1.0]])]});}
            var Q56;
            {var subQ0=sQuery(id+"F0.wireOp",EDGE,"E19.trimOffspring");var subQ1=sQuery(id+"F0.wireOp",EDGE,"E12");var subQ2=makeQuery(id+"F0.imprint","INTERSECT",VERTEX,{"derivedFrom":[subQ1,subQ0]});Q56=makeQuery(id+"F0.imprint","IMPRINT",FACE,{"disambiguationData":[TD([[makeQuery(id+"F0.imprint","IMPRINT",EDGE,{"disambiguationData":[TD([[subQ2,1.0]])],"derivedFrom":subQ1}),1.0]])]});}
            var Q57;
            {var subQ0=sQuery(id+"F0.wireOp",EDGE,"E11");var subQ1=sQuery(id+"F0.wireOp",EDGE,"E0.bottom");var subQ2=makeQuery(id+"F0.imprint","INTERSECT",VERTEX,{"derivedFrom":[subQ1,subQ0]});Q57=makeQuery(id+"F0.imprint","IMPRINT",FACE,{"disambiguationData":[TD([[makeQuery(id+"F0.imprint","IMPRINT",EDGE,{"disambiguationData":[TD([[subQ2,1.0]])],"derivedFrom":subQ1}),-1.0]])]});}
            var Q58;
            {var subQ0=sQuery(id+"F0.wireOp",EDGE,"E31");var subQ1=sQuery(id+"F0.wireOp",EDGE,"E9");var subQ2=makeQuery(id+"F0.imprint","INTERSECT",VERTEX,{"derivedFrom":[subQ1,subQ0]});Q58=makeQuery(id+"F0.imprint","IMPRINT",FACE,{"disambiguationData":[TD([[makeQuery(id+"F0.imprint","IMPRINT",EDGE,{"disambiguationData":[TD([[subQ2,-1.0]])],"derivedFrom":subQ1}),-1.0]])]});}
            var Q59;
            {var subQ0=sQuery(id+"F0.wireOp",EDGE,"E16");var subQ1=sQuery(id+"F0.wireOp",EDGE,"E0.top");var subQ2=makeQuery(id+"F0.imprint","INTERSECT",VERTEX,{"derivedFrom":[subQ1,subQ0]});Q59=makeQuery(id+"F0.imprint","IMPRINT",FACE,{"disambiguationData":[TD([[makeQuery(id+"F0.imprint","IMPRINT",EDGE,{"disambiguationData":[TD([[subQ2,-1.0]])],"derivedFrom":subQ1}),1.0]])]});}
            var Q60;
            {var subQ0=sQuery(id+"F0.wireOp",EDGE,"E12");var subQ1=sQuery(id+"F0.wireOp",EDGE,"E0.bottom");var subQ2=makeQuery(id+"F0.imprint","INTERSECT",VERTEX,{"derivedFrom":[subQ1,subQ0]});Q60=makeQuery(id+"F0.imprint","IMPRINT",FACE,{"disambiguationData":[TD([[makeQuery(id+"F0.imprint","IMPRINT",EDGE,{"disambiguationData":[TD([[subQ2,-1.0]])],"derivedFrom":subQ1}),-1.0]])]});}
            var Q61;
            {var subQ0=sQuery(id+"F0.wireOp",EDGE,"E16");var subQ1=sQuery(id+"F0.wireOp",EDGE,"E0.top");var subQ2=makeQuery(id+"F0.imprint","INTERSECT",VERTEX,{"derivedFrom":[subQ1,subQ0]});Q61=makeQuery(id+"F0.imprint","IMPRINT",FACE,{"disambiguationData":[TD([[makeQuery(id+"F0.imprint","IMPRINT",EDGE,{"disambiguationData":[TD([[subQ2,1.0]])],"derivedFrom":subQ1}),1.0]])]});}
            var Q62;
            {var subQ1=sQuery(id+"F0.wireOp",EDGE,"E9");var subQ3=sQuery(id+"F0.wireOp",EDGE,"E35");var subQ4=makeQuery(id+"F0.imprint","INTERSECT",VERTEX,{"derivedFrom":[subQ1,subQ3]});Q62=makeQuery(id+"F0.imprint","IMPRINT",FACE,{"disambiguationData":[TD([[makeQuery(id+"F0.imprint","IMPRINT",EDGE,{"disambiguationData":[TD([[subQ4,-1.0]])],"derivedFrom":subQ3}),-1.0]])]});}
            var Q63;
            {var subQ0=sQuery(id+"F0.wireOp",EDGE,"E17");Q63=makeQuery(id+"F0.imprint","IMPRINT",FACE,{"disambiguationData":[TD([[makeQuery(id+"F0.imprint","IMPRINT",EDGE,{"derivedFrom":subQ0}),-1.0]])]});}
            extrude(context, id + "F1", {"entities" : qUnion([Q0, Q1, Q2, Q3, Q4, Q5, Q6, Q7, Q8, Q9, Q10, Q11, Q12, Q13, Q14, Q15, Q16, Q17, Q18, Q19, Q20, Q21, Q22, Q23, Q24, Q25, Q26, Q27, Q28, Q29, Q30, Q31, Q32, Q33, Q34, Q35, Q36, Q37, Q38, Q39, Q40, Q41, Q42, Q43, Q44, Q45, Q46, Q47, Q48, Q49, Q50, Q51, Q52, Q53, Q54, Q55, Q56, Q57, Q58, Q59, Q60, Q61, Q62, Q63]), "oppositeDirection" : true, "depth" : 0.15 * mm, "offsetDistance" : 25 * mm});
        }
    });
